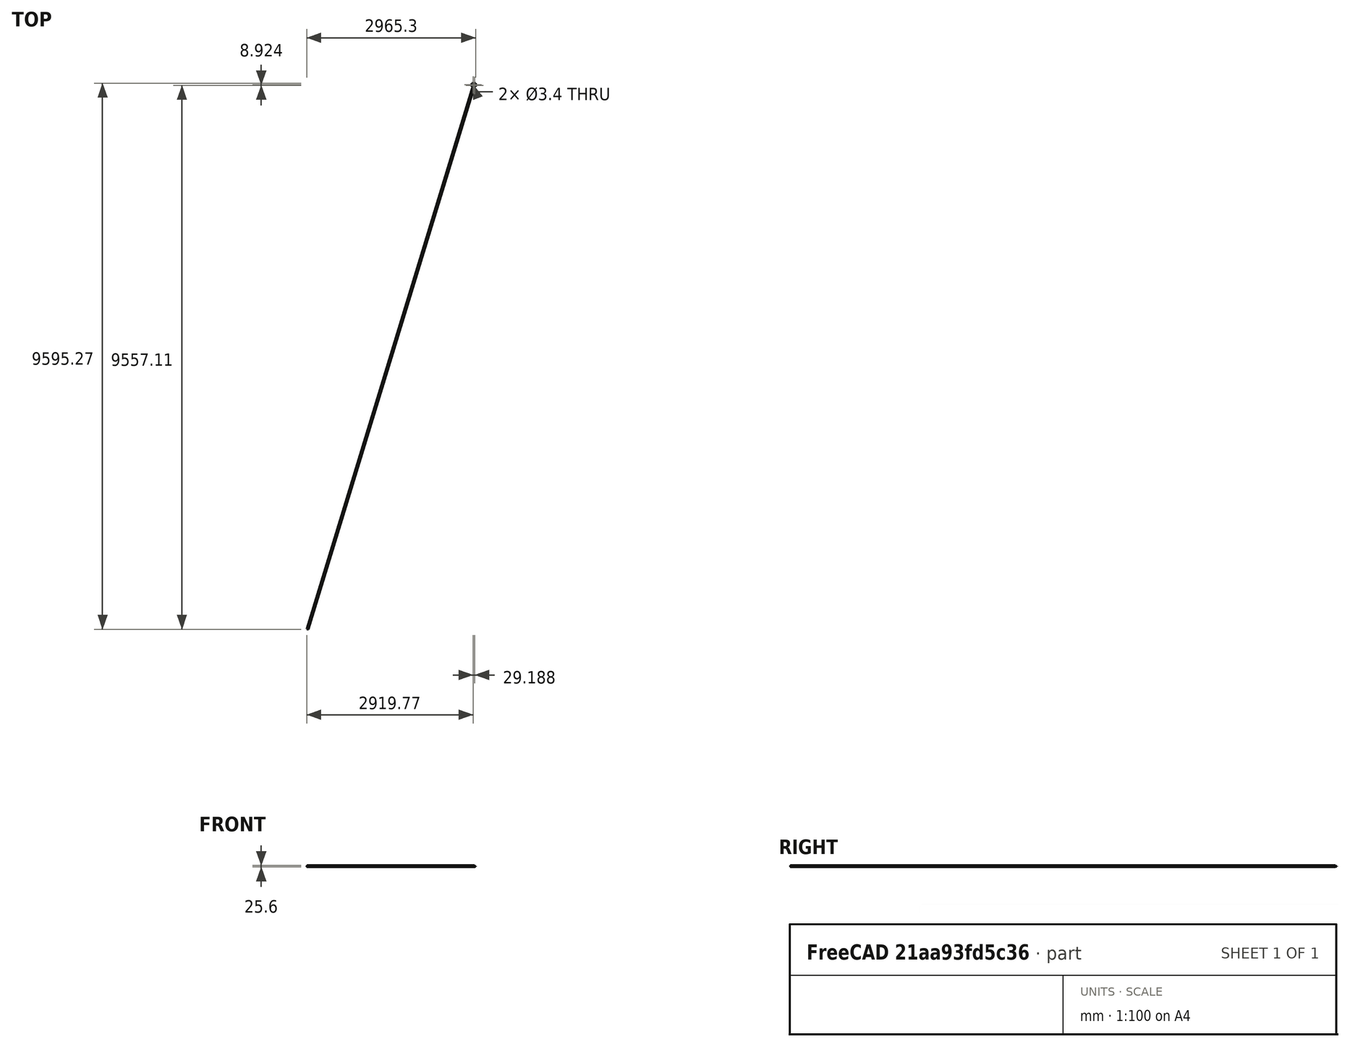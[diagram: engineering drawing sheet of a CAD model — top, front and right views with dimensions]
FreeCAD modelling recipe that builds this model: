
FCSTD DOCUMENT  (FreeCAD 0.16R)
Label: cap3
License: All rights reserved
LicenseURL: http://en.wikipedia.org/wiki/All_rights_reserved
objects: Sketcher::SketchObject×4, PartDesign::Pocket×3, PartDesign::Pad×1, PartDesign::Fillet×1, Mesh::Feature×1
note: 13 computed .brp shape members not serialized (recipe doc carries the construction recipe); baked Part::Feature solids carry a one-line shape summary decoded from their .brp

FEATURE [Sketcher::SketchObject] Sketch002
  Placement = pos=(0,0,4) rot=(0,0,1;0rad)
  sketch-geometry (5):
    g0: LineSegment [constr] StartX=-6 StartY=0 StartZ=0 EndX=37.8558 EndY=143.446 EndZ=0
    g1: LineSegment StartX=-5.67118 StartY=62.641 StartZ=0 EndX=28.7558 EndY=52.1156 EndZ=0
    g2: LineSegment StartX=28.7558 StartY=52.1156 StartZ=0 EndX=25.2473 EndY=40.6399 EndZ=0
    g3: LineSegment StartX=25.2473 StartY=40.6399 StartZ=0 EndX=-9.17964 EndY=51.1653 EndZ=0
    g4: LineSegment StartX=-9.17964 StartY=51.1653 StartZ=0 EndX=-5.67118 EndY=62.641 EndZ=0
  constraints (16):
    c: Distance(g0) = 150
    c: Angle(g0) = 1.27409
    c: Coincident(g1,g2)
    c: Coincident(g2,g3)
    c: Coincident(g3,g4)
    c: Coincident(g4,g1)
    c: Perpendicular(g0,g3)
    c: Perpendicular(g0,g1)
    c: Parallel(g4,g0)
    c: Parallel(g2,g0)
    c: Symmetric(g2,g3,g0)
    c: Distance(g2) = 12
    c: Distance(g1) = 36
    c: PointOnObject(g0,g-1)
    c: Distance(g-1,g0) = 6
    c: Distance(g0,g3) = 48
FEATURE [PartDesign::Pad] Pad
  Length = 16
  Length2 = 100
  Placement = pos=(0,0,4) rot=(0,0,1;0rad)
  Sketch = -> Sketch002
  Type = 0
FEATURE [Sketcher::SketchObject] Sketch
  ExternalGeometry = -> [Pad]
  Placement = pos=(17.0294,55.7007,4) rot=(0.105093,0.703191,0.703191;2.93218rad)
  Support = -> Pad [Face1]
  sketch-geometry (1):
    g0: Circle CenterX=5.73783 CenterY=16 CenterZ=0 NormalX=0 NormalY=0 NormalZ=1 Radius=12.8
  constraints (2):
    c: Radius(g0) = 12.8
    c: Symmetric(g-3,g-3,g0)
FEATURE [PartDesign::Pocket] Pocket
  Length = 5
  Placement = pos=(0,0,4) rot=(0,0,1;0rad)
  Sketch = -> Sketch
  Type = 1
FEATURE [Sketcher::SketchObject] Sketch003
  Placement = pos=(0,0,20) rot=(0,0,1;0rad)
  Support = -> Pocket [Face4]
  sketch-geometry (4):
    g0: LineSegment StartX=-28.4516 StartY=85.8592 StartZ=0 EndX=40.8759 EndY=85.8592 EndZ=0
    g1: LineSegment StartX=40.8759 StartY=85.8592 StartZ=0 EndX=40.8759 EndY=28.3375 EndZ=0
    g2: LineSegment StartX=40.8759 StartY=28.3375 StartZ=0 EndX=-28.4516 EndY=28.3375 EndZ=0
    g3: LineSegment StartX=-28.4516 StartY=28.3375 StartZ=0 EndX=-28.4516 EndY=85.8592 EndZ=0
  constraints (8):
    c: Coincident(g0,g1)
    c: Coincident(g1,g2)
    c: Coincident(g2,g3)
    c: Coincident(g3,g0)
    c: Horizontal(g0)
    c: Horizontal(g2)
    c: Vertical(g1)
    c: Vertical(g3)
FEATURE [PartDesign::Pocket] Pocket001
  Length = 1
  Placement = pos=(0,0,4) rot=(0,0,1;0rad)
  Sketch = -> Sketch003
  Type = 0
FEATURE [Sketcher::SketchObject] Sketch004
  ExternalGeometry = -> [Pocket001]
  Placement = pos=(0,0,19) rot=(0,0,1;0rad)
  Support = -> Pocket001 [Face4]
  sketch-geometry (2):
    g0: Circle CenterX=24.5417 CenterY=47.7004 CenterZ=0 NormalX=0 NormalY=0 NormalZ=1 Radius=1.7
    g1: Circle CenterX=-4.64645 CenterY=56.6241 CenterZ=0 NormalX=0 NormalY=0 NormalZ=1 Radius=1.7
  constraints (6):
    c: Radius(g1) = 1.7
    c: Equal(g1,g0)
    c: Distance(g0,g-6) = 6
    c: Distance(g1,g-4) = 6
    c: Distance(g1,g-4) = 2.5
    c: Distance(g0,g-5) = 2.5
FEATURE [PartDesign::Pocket] Pocket002
  Length = 5
  Placement = pos=(0,0,4) rot=(0,0,1;0rad)
  Sketch = -> Sketch004
  Type = 1
FEATURE [PartDesign::Fillet] Fillet
  Base = -> Pocket002 [Edge2,Edge12,Edge6,Edge22]
  Placement = pos=(0,0,4) rot=(0,0,1;0rad)
  Radius = 1
FEATURE [Mesh::Feature] Mesh  label="Fillet (Meshed)"
